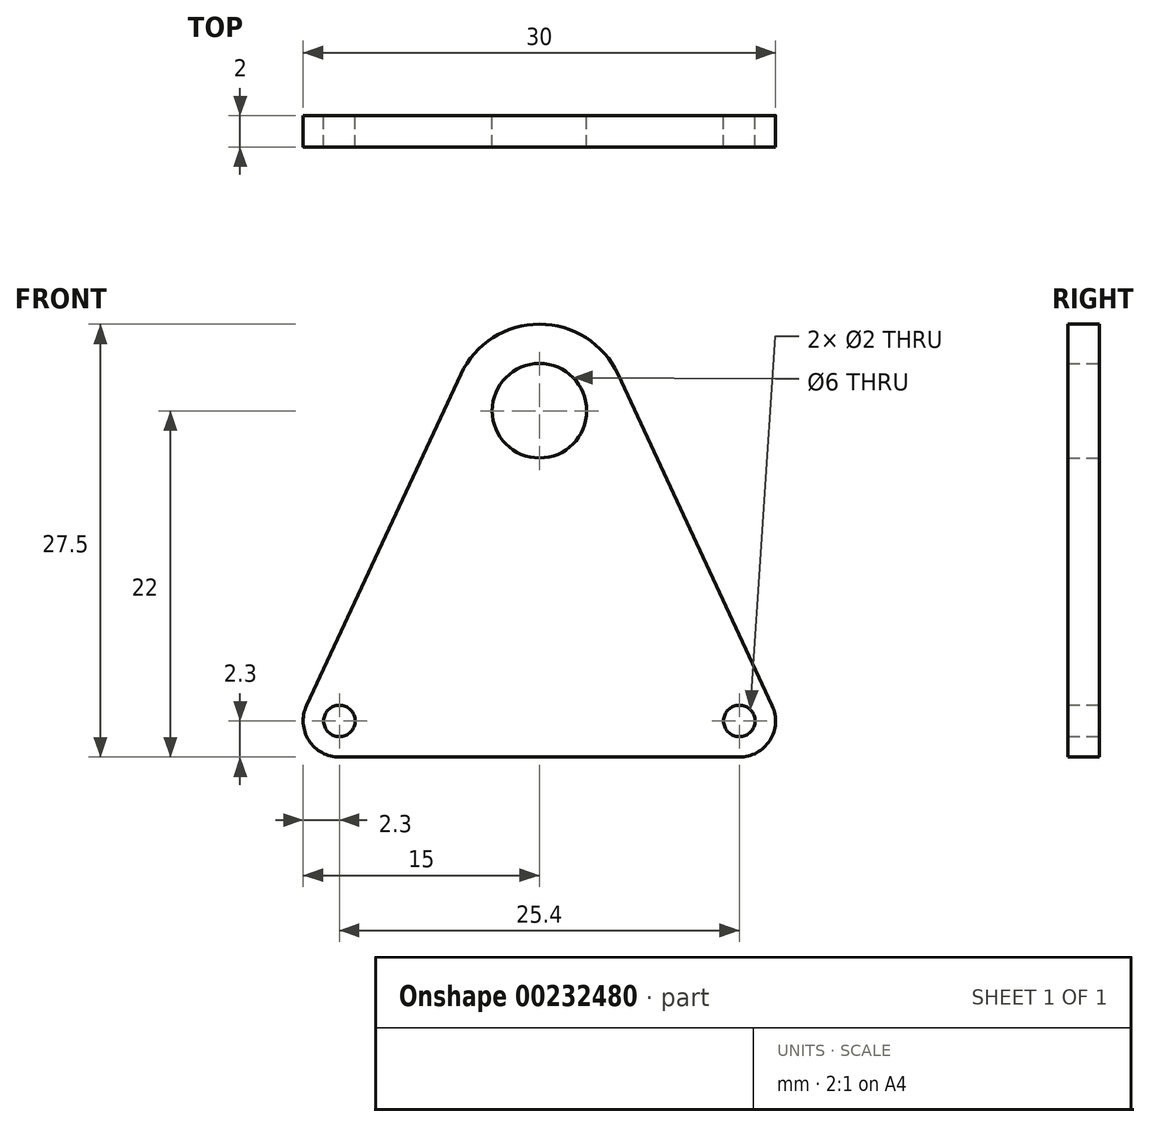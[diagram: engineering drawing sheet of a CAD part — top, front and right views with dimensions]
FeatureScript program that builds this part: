
annotation { "Feature Type Name" : "Feature", "Feature Type Description" : "" }
export const myFeature = defineFeature(function(context is Context, id is Id, definition is map)
    precondition{}
    {
        {
            var Q0;
            Q0=qCreatedBy(makeId("Front.planeOp"),FACE);
            var sketch = newSketch(context, id + "F0", { "sketchPlane" : qUnion([Q0])});
            skArc(sketch, "E0", {"start": v(0, 19) * mm, "mid": v(3, 22) * mm, "end": v(0, 25) * mm});
            skArc(sketch, "E1", {"start": v(4.99, 24.32) * mm, "mid": v(2.96, 26.64) * mm, "end": v(0, 27.5) * mm});
            skLineSegment(sketch, "E2", {"start": v(0, 0) * mm, "end": v(12.7, 0) * mm});
            skCircle(sketch, "E3", {"center": v(12.7, 2.3) * mm, "radius": 1 * mm});
            skArc(sketch, "E4", {"start": v(12.7, 0) * mm, "mid": v(14.64, 1.06) * mm, "end": v(14.79, 3.27) * mm});
            skLineSegment(sketch, "E5", {"start": v(4.99, 24.32) * mm, "end": v(14.79, 3.27) * mm});
            skArc(sketch, "E6.MirrorCS", {"start": v(0, 19) * mm, "mid": v(-3, 22) * mm, "end": v(0, 25) * mm});
            skArc(sketch, "E7.MirrorCS", {"start": v(-4.99, 24.32) * mm, "mid": v(-2.96, 26.64) * mm, "end": v(0, 27.5) * mm});
            skLineSegment(sketch, "E8.MirrorCS", {"start": v(-4.99, 24.32) * mm, "end": v(-14.79, 3.27) * mm});
            skCircle(sketch, "E9.MirrorC", {"center": v(-12.7, 2.3) * mm, "radius": 1 * mm});
            skLineSegment(sketch, "E10.MirrorCS", {"start": v(0, 0) * mm, "end": v(-12.7, 0) * mm});
            skArc(sketch, "E11.MirrorCS", {"start": v(-12.7, 0) * mm, "mid": v(-14.64, 1.06) * mm, "end": v(-14.79, 3.27) * mm});
            skSolve(sketch);
        }
        {
            var Q0;
            Q0=makeQuery(id+"F0.imprint","IMPRINT",FACE,{"disambiguationData":[TD([[makeQuery(id+"F0.imprint","IMPRINT",EDGE,{"derivedFrom":sQuery(id+"F0.wireOp",EDGE,"E0")}),-1.0]])]});
            extrude(context, id + "F1", {"entities" : qUnion([Q0]), "depth" : 2 * mm});
        }
    });
